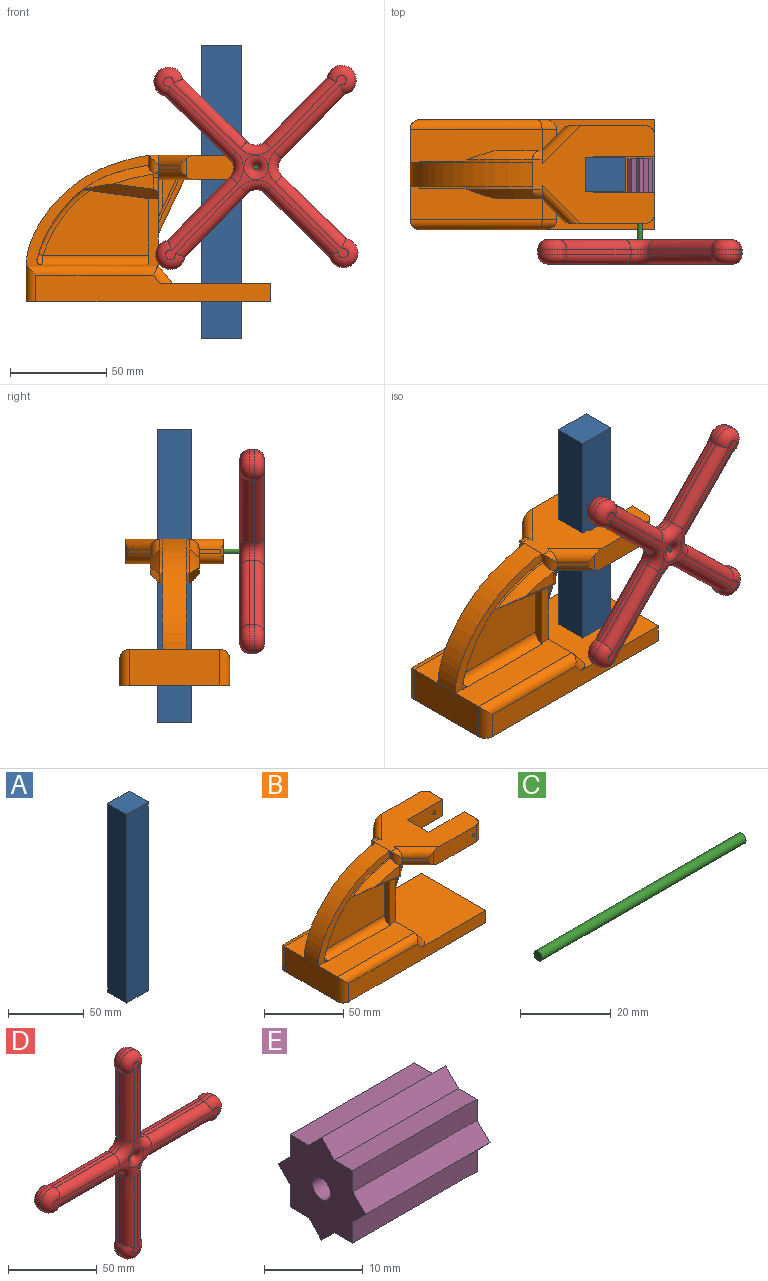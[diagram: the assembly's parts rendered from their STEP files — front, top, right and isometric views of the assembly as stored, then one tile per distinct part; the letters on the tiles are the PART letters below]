
ASSEMBLY  parts=5 mates=4
PART A: 6 faces, bbox 20.3x17.8x152.4 mm
  f0: plane 152.4x20.32mm, normal (0,1,0), area 3096.8mm2, adj f1,f3,f4,f5
  f1: plane 20.32x17.78mm, normal (0,0,1), area 361.3mm2, adj f0,f2,f4,f5
  f2: plane 152.4x20.32mm, normal (0,-1,0), area 3096.8mm2, adj f1,f3,f4,f5
  f3: plane 20.32x17.78mm, normal (0,0,-1), area 361.3mm2, adj f0,f2,f4,f5
  f4: plane 152.4x17.78mm, normal (1,0,0), area 2709.7mm2, adj f0,f1,f2,f3
  f5: plane 152.4x17.78mm, normal (-1,0,0), area 2709.7mm2, adj f0,f1,f2,f3
PART B: 93 faces, bbox 129.2x60.2x85.1 mm
  f0: plane 47.9x22.57mm, normal (1,0,0), area 413.4mm2, adj f1,f2,f12,f37,f38,f39,f45,f50
  f1: plane 58.93x51.31mm, normal (0,0,-1), area 1893.8mm2, adj f0,f2,f3,f57,f58,f59,f62,f67
  f2: plane 21.89x11.58mm, normal (-0.9,0,0.43), area 68.6mm2, adj f0,f1,f76,f78,f83
  f3: plane 12.7x10.8mm, normal (1,0,0), area 137.1mm2, adj f1,f46,f69,f71
  f4: plane 68.58x17.15mm, normal (0,0,1), area 1138.7mm2, adj f6,f7,f8,f12,f19,f22,f33,f38
  f5: plane 68.58x17.15mm, normal (0,0,1), area 1138.7mm2, adj f8,f12,f15,f16,f20,f25,f32,f37
  f6: plane 0.64x0.04mm, normal (1,0,0), area 0mm2, adj f4,f19,f38
  f7: extruded ~0.64x0.04mm, area 0mm2, adj f4,f19,f33
  f8: plane 46.99x19.05mm, normal (-1,0,0), area 895.2mm2, adj f4,f5,f9,f23,f26,f30
  f9: plane 127x57.15mm, normal (0,0,-1), area 7247mm2, adj f8,f10,f13,f14,f23,f26
  f10: plane 57.15x9.53mm, normal (1,0,0), area 544.4mm2, adj f9,f11,f13,f14
  f11: plane 59.01x58.86mm, normal (0,0,1), area 2917.4mm2, adj f10,f12,f13,f14,f21,f24
  f12: plane 46.99x9.53mm, normal (0.78,0,0.62), area 573.2mm2, adj f0,f4,f5,f11,f21,f24
  f13: plane 121.92x13.97mm, normal (0,-1,0), area 1440.6mm2, adj f9,f10,f11,f24,f25,f26
  f14: plane 121.92x13.97mm, normal (0,1,0), area 1440.6mm2, adj f9,f10,f11,f21,f22,f23
  f15: plane 0.64x0.04mm, normal (1,0,0), area 0mm2, adj f5,f20,f37
  f16: extruded ~0.64x0.04mm, area 0mm2, adj f5,f20,f32
  f17: plane 54.64x33.76mm, normal (0,-1,0), area 1467.7mm2, adj f20,f27,f29,f79
  f18: plane 54.64x33.76mm, normal (0,1,0), area 1467.7mm2, adj f19,f36,f44,f81
  f19: cylinder r=5.08mm len=58.42mm, axis (1,0,0), area 440.8mm2, adj f4,f6,f7,f18,f33,f36,f82
  f20: cylinder r=5.08mm len=58.42mm, axis (-1,0,0), area 440.8mm2, adj f5,f15,f16,f17,f29,f32,f80
  f21: cylinder r=5.08mm len=12.7mm, axis (-0.62,0,0.78), area 71.4mm2, adj f11,f12,f14,f22
  f22: cylinder r=5.08mm len=68.58mm, axis (-1,0,0), area 517.2mm2, adj f4,f14,f21,f23
  f23: cylinder r=5.08mm len=19.05mm, axis (0,0,-1), area 131.7mm2, adj f8,f9,f14,f22
  f24: cylinder r=5.08mm len=12.7mm, axis (0.62,0,-0.78), area 71.4mm2, adj f11,f12,f13,f25
  f25: cylinder r=5.08mm len=68.58mm, axis (1,0,0), area 517.2mm2, adj f5,f13,f24,f26
  f26: cylinder r=5.08mm len=19.05mm, axis (0,0,1), area 131.7mm2, adj f8,f9,f13,f25
  f27: plane 35.02x6.64mm, normal (-0.14,0,-0.99), area 194.7mm2, adj f17,f28,f29,f39,f43,f52,f79
  f28: extruded ~36.1x23.66mm, area 81.2mm2, adj f27,f32,f79,f80
  f29: plane 34.61x4.45mm, normal (-1,0,0), area 148.5mm2, adj f17,f20,f27,f37
  f30: extruded ~63.5x57.15mm, area 1168.6mm2, adj f8,f32,f33,f46
  f31: extruded ~36.1x23.66mm, area 81.2mm2, adj f33,f44,f81,f82
  f32: plane 63.96x57.61mm, normal (0,-1,0), area 447.1mm2, adj f5,f16,f20,f28,f30,f34,f43,f80
  f33: plane 63.96x57.61mm, normal (0,1,0), area 447.1mm2, adj f4,f7,f19,f30,f31,f35,f42,f82
  f34: plane 5.08x1.27mm, normal (-1,0,0), area 6.5mm2, adj f32,f43,f46,f55
  f35: extruded ~34.1x12.76mm, area 46.7mm2, adj f33,f42,f44,f49
  f36: plane 34.61x4.45mm, normal (-1,0,0), area 148.5mm2, adj f18,f19,f38,f44
  f37: plane 34.65x5.08mm, normal (0,-1,0), area 176mm2, adj f0,f5,f15,f29,f39
  f38: plane 34.65x5.08mm, normal (0,1,0), area 176mm2, adj f0,f4,f6,f36,f45
  f39: plane 5.08x1.96mm, normal (0,0,-1), area 8.2mm2, adj f0,f27,f37,f52
  f40: plane 9.32x7.22mm, normal (1,0,0), area 2.3mm2, adj f46,f56,f65
  f41: plane 9.32x7.22mm, normal (1,0,0), area 2.3mm2, adj f46,f54,f63
  f42: plane 5.08x1.27mm, normal (-1,0,0), area 6.5mm2, adj f33,f35,f46,f53
  f43: extruded ~34.1x12.76mm, area 46.7mm2, adj f27,f32,f34,f51
  f44: plane 35.02x6.64mm, normal (-0.14,0,-0.99), area 194.7mm2, adj f18,f31,f35,f36,f45,f50,f81
  f45: plane 5.08x1.96mm, normal (0,0,-1), area 8.2mm2, adj f0,f38,f44,f50
  f46: plane 63.5x50.8mm, normal (0,0,1), area 2033.9mm2, adj f3,f30,f34,f40,f41,f42,f54,f56
  f47: plane 22.05x8.82mm, normal (0,-1,0), area 89.7mm2, adj f51,f52,f87,f88
  f48: plane 22.05x8.82mm, normal (0,1,0), area 89.7mm2, adj f49,f50,f89,f90
  f49: bspline ~38.17x17.36mm, area 205.8mm2, adj f35,f48,f50,f53,f89
  f50: plane 40.23x8.67mm, normal (-0.1,0.71,-0.7), area 226.6mm2, adj f0,f44,f45,f48,f49,f90
  f51: bspline ~39.92x18.11mm, area 205.8mm2, adj f43,f47,f52,f55,f87
  f52: plane 40.24x8.68mm, normal (-0.1,-0.71,-0.7), area 226.7mm2, adj f0,f27,f39,f47,f51,f88
  f53: cylinder r=5.08mm len=9.41mm, axis (0,0,-1), area 44.4mm2, adj f42,f49,f54,f61,f89
  f54: cylinder r=5.08mm len=5.08mm, axis (-1,0,0), area 20.3mm2, adj f41,f46,f53
  f55: cylinder r=5.08mm len=9.41mm, axis (0,0,1), area 44.4mm2, adj f34,f51,f56,f60,f87
  f56: cylinder r=5.08mm len=5.08mm, axis (1,0,0), area 20.3mm2, adj f40,f46,f55
  f57: plane 12.7x10.8mm, normal (1,0,0), area 137.1mm2, adj f1,f46,f68,f70
  f58: plane 38.84x13mm, normal (0,-1,0), area 479.6mm2, adj f1,f46,f65,f66,f67,f69,f91
  f59: plane 38.84x13mm, normal (0,1,0), area 479.6mm2, adj f1,f46,f62,f63,f64,f68,f92
  f60: plane 11.21x11.21mm, normal (-0.71,-0.71,0), area 40.3mm2, adj f55,f65,f66,f67
  f61: plane 11.21x11.21mm, normal (-0.71,0.71,0), area 40.3mm2, adj f53,f62,f63,f64
  f62: cylinder r=5.08mm len=23.48mm, axis (-0.71,-0.71,0), area 171.4mm2, adj f0,f1,f59,f61,f64,f89
  f63: cylinder r=5.08mm len=23.48mm, axis (-0.71,-0.71,0), area 175.5mm2, adj f41,f46,f59,f61,f64
  f64: cylinder r=5.08mm len=9.72mm, axis (0,0,-1), area 24.5mm2, adj f59,f61,f62,f63
  f65: cylinder r=5.08mm len=23.48mm, axis (-0.71,0.71,0), area 175.5mm2, adj f40,f46,f58,f60,f66
  f66: cylinder r=5.08mm len=9.72mm, axis (0,0,1), area 24.5mm2, adj f58,f60,f65,f67
  f67: cylinder r=5.08mm len=23.48mm, axis (-0.71,0.71,0), area 171.4mm2, adj f0,f1,f58,f60,f66,f87
  f68: cylinder r=5.08mm len=12.7mm, axis (0,0,1), area 101.3mm2, adj f1,f46,f57,f59
  f69: cylinder r=5.08mm len=12.7mm, axis (0,0,-1), area 101.3mm2, adj f1,f3,f46,f58
  f70: plane 31.75x12.7mm, normal (0,-1,0), area 398.2mm2, adj f1,f46,f57,f72,f92
  f71: plane 31.75x12.7mm, normal (0,1,0), area 398.2mm2, adj f1,f3,f46,f72,f91
  f72: plane 19.05x12.7mm, normal (1,0,0), area 241.9mm2, adj f1,f46,f70,f71
  f73: plane 21.89x11.58mm, normal (-0.9,0,0.43), area 68.6mm2, adj f0,f1,f75,f77,f84
  f74: plane 28.68x13.63mm, normal (0.9,0,-0.43), area 129mm2, adj f0,f1,f85,f86
  f75: plane 22.76x10.81mm, normal (0,-1,0), area 31.4mm2, adj f0,f1,f73,f86
  f76: plane 22.76x10.81mm, normal (0,1,0), area 31.4mm2, adj f0,f1,f2,f85
  f77: plane 14.3x6.79mm, normal (0,-1,0), area 48.5mm2, adj f1,f73,f84
  f78: plane 14.3x6.79mm, normal (0,1,0), area 48.5mm2, adj f1,f2,f83
  f79: bspline ~60.99x57.21mm, area 167.4mm2, adj f17,f27,f28,f80
  f80: bspline ~6.54x5.32mm, area 26.1mm2, adj f20,f28,f32,f79
  f81: bspline ~60.99x57.21mm, area 167.4mm2, adj f18,f31,f44,f82
  f82: bspline ~6.54x5.32mm, area 26.1mm2, adj f19,f31,f33,f81
  f83: cylinder r=2.54mm len=19.64mm, axis (0,0,-1), area 67.7mm2, adj f0,f1,f2,f78
  f84: cylinder r=2.54mm len=19.64mm, axis (0,0,1), area 67.7mm2, adj f0,f1,f73,f77
  f85: cylinder r=2.54mm len=29.77mm, axis (0.43,0,0.9), area 113.6mm2, adj f0,f1,f74,f76
  f86: cylinder r=2.54mm len=29.77mm, axis (-0.43,0,-0.9), area 113.6mm2, adj f0,f1,f74,f75
  f87: bspline ~4.48x2.81mm, area 6.4mm2, adj f47,f51,f55,f67,f88
  f88: cylinder r=2.54mm len=9.13mm, axis (0,0,-1), area 30.6mm2, adj f0,f47,f52,f87
  f89: bspline ~4.48x2.81mm, area 7.3mm2, adj f48,f49,f53,f62,f90
  f90: cylinder r=2.54mm len=9.13mm, axis (0,0,1), area 30.6mm2, adj f0,f48,f50,f89
  f91: cylinder r=1.27mm len=15.88mm, axis (0,-1,0), area 126.7mm2, adj f58,f71
  f92: cylinder r=1.27mm len=15.88mm, axis (0,-1,0), area 126.7mm2, adj f59,f70
PART C: 3 faces, bbox 63.5x2.5x2.5 mm
  f0: cylinder r=1.27mm len=63.5mm, axis (-1,0,0), area 506.7mm2, adj f1,f2
  f1: plane 2.54x2.54mm, normal (1,0,0), area 5.1mm2, adj f0
  f2: plane 2.54x2.54mm, normal (-1,0,0), area 5.1mm2, adj f0
PART D: 53 faces, bbox 142.2x12.7x142.2 mm
  f0: cylinder r=7.62mm len=15.24mm, axis (0,1,0), area 83.5mm2, adj f1,f15,f32,f49
  f1: plane 46.59x2.54mm, normal (1,0,0), area 118.3mm2, adj f0,f2,f30,f47
  f2: cylinder r=6.35mm len=6.35mm, axis (0,1,0), area 25.3mm2, adj f1,f3,f28,f45
  f3: plane 46.59x2.54mm, normal (0,0,-1), area 118.3mm2, adj f2,f4,f26,f43
  f4: cylinder r=7.62mm len=15.24mm, axis (0,1,0), area 83.5mm2, adj f3,f5,f24,f41
  f5: plane 46.59x2.54mm, normal (0,0,1), area 118.3mm2, adj f4,f6,f22,f39
  f6: cylinder r=6.35mm len=6.35mm, axis (0,1,0), area 25.3mm2, adj f5,f7,f20,f37
  f7: plane 46.59x2.54mm, normal (1,0,0), area 118.3mm2, adj f6,f8,f19,f36
  f8: cylinder r=7.62mm len=15.24mm, axis (0,1,0), area 83.5mm2, adj f7,f9,f21,f38
  f9: plane 46.59x2.54mm, normal (-1,0,0), area 118.3mm2, adj f8,f10,f23,f40
  f10: cylinder r=6.35mm len=6.35mm, axis (0,1,0), area 25.3mm2, adj f9,f11,f25,f42
  f11: plane 46.59x2.54mm, normal (0,0,1), area 118.3mm2, adj f10,f12,f27,f44
  f12: cylinder r=7.62mm len=15.24mm, axis (0,1,0), area 83.5mm2, adj f11,f13,f29,f46
  f13: plane 46.59x2.54mm, normal (0,0,-1), area 118.3mm2, adj f12,f14,f31,f48
  f14: cylinder r=6.35mm len=6.35mm, axis (0,1,0), area 25.3mm2, adj f13,f15,f33,f50
  f15: plane 46.59x2.54mm, normal (-1,0,0), area 118.3mm2, adj f0,f14,f34,f51
  f16: cylinder r=1.27mm len=2.54mm, axis (0,1,0), area 20.3mm2, adj f35,f52
  f17: plane 132.08x132.08mm, normal (0,-1,0), area 680.6mm2, adj f36,f37,f38,f39,f40,f41,f42,f43
  f18: plane 132.08x132.08mm, normal (0,1,0), area 680.6mm2, adj f19,f20,f21,f22,f23,f24,f25,f26
  f19: cylinder r=5.08mm len=48.6mm, axis (0,0,1), area 376.9mm2, adj f7,f18,f20,f21
  f20: torus R=11.43mm, axis (0,-1,0), area 102.7mm2, adj f6,f18,f19,f22
  f21: torus R=2.54mm, axis (0,-1,0), area 206.5mm2, adj f8,f18,f19,f23
  f22: cylinder r=5.08mm len=48.6mm, axis (-1,0,0), area 376.9mm2, adj f5,f18,f20,f24
  f23: cylinder r=5.08mm len=48.6mm, axis (0,0,-1), area 376.9mm2, adj f9,f18,f21,f25
  f24: torus R=2.54mm, axis (0,-1,0), area 206.5mm2, adj f4,f18,f22,f26
  f25: torus R=11.43mm, axis (0,-1,0), area 102.7mm2, adj f10,f18,f23,f27
  f26: cylinder r=5.08mm len=48.6mm, axis (1,0,0), area 376.9mm2, adj f3,f18,f24,f28
  f27: cylinder r=5.08mm len=48.6mm, axis (-1,0,0), area 376.9mm2, adj f11,f18,f25,f29
  f28: torus R=11.43mm, axis (0,-1,0), area 102.7mm2, adj f2,f18,f26,f30
  f29: torus R=2.54mm, axis (0,-1,0), area 206.5mm2, adj f12,f18,f27,f31
  f30: cylinder r=5.08mm len=48.6mm, axis (0,0,1), area 376.9mm2, adj f1,f18,f28,f32
  f31: cylinder r=5.08mm len=48.6mm, axis (1,0,0), area 376.9mm2, adj f13,f18,f29,f33
  f32: torus R=2.54mm, axis (0,-1,0), area 206.5mm2, adj f0,f18,f30,f34
  f33: torus R=11.43mm, axis (0,-1,0), area 102.7mm2, adj f14,f18,f31,f34
  f34: cylinder r=5.08mm len=48.6mm, axis (0,0,-1), area 376.9mm2, adj f15,f18,f32,f33
  f35: torus R=6.35mm, axis (0,-1,0), area 156.2mm2, adj f16,f18
  f36: cylinder r=5.08mm len=48.6mm, axis (0,0,-1), area 376.9mm2, adj f7,f17,f37,f38
  f37: torus R=11.43mm, axis (0,-1,0), area 102.7mm2, adj f6,f17,f36,f39
  f38: torus R=2.54mm, axis (0,-1,0), area 206.5mm2, adj f8,f17,f36,f40
  f39: cylinder r=5.08mm len=48.6mm, axis (1,0,0), area 376.9mm2, adj f5,f17,f37,f41
  f40: cylinder r=5.08mm len=48.6mm, axis (0,0,1), area 376.9mm2, adj f9,f17,f38,f42
  f41: torus R=2.54mm, axis (0,-1,0), area 206.5mm2, adj f4,f17,f39,f43
  f42: torus R=11.43mm, axis (0,-1,0), area 102.7mm2, adj f10,f17,f40,f44
  f43: cylinder r=5.08mm len=48.6mm, axis (-1,0,0), area 376.9mm2, adj f3,f17,f41,f45
  f44: cylinder r=5.08mm len=48.6mm, axis (1,0,0), area 376.9mm2, adj f11,f17,f42,f46
  f45: torus R=11.43mm, axis (0,-1,0), area 102.7mm2, adj f2,f17,f43,f47
  f46: torus R=2.54mm, axis (0,-1,0), area 206.5mm2, adj f12,f17,f44,f48
  f47: cylinder r=5.08mm len=48.6mm, axis (0,0,-1), area 376.9mm2, adj f1,f17,f45,f49
  f48: cylinder r=5.08mm len=48.6mm, axis (-1,0,0), area 376.9mm2, adj f13,f17,f46,f50
  f49: torus R=2.54mm, axis (0,-1,0), area 206.5mm2, adj f0,f17,f47,f51
  f50: torus R=11.43mm, axis (0,-1,0), area 102.7mm2, adj f14,f17,f48,f51
  f51: cylinder r=5.08mm len=48.6mm, axis (0,0,1), area 376.9mm2, adj f15,f17,f49,f50
  f52: torus R=6.35mm, axis (0,-1,0), area 156.2mm2, adj f16,f17
PART E: 19 faces, bbox 17.8x12.6x12.7 mm
  f0: plane 17.78x1.86mm, normal (0,-0.71,-0.71), area 46.8mm2, adj f1,f15,f17,f18
  f1: plane 17.78x1.86mm, normal (0,0.71,-0.7), area 46.3mm2, adj f0,f2,f17,f18
  f2: plane 17.78x2.67mm, normal (0,0,-1), area 47.4mm2, adj f1,f3,f17,f18
  f3: plane 17.78x2.72mm, normal (0,1,0), area 48.4mm2, adj f2,f4,f17,f18
  f4: plane 17.78x1.77mm, normal (0,0.71,-0.7), area 44mm2, adj f3,f5,f17,f18
  f5: plane 17.78x1.77mm, normal (0,0.71,0.7), area 44mm2, adj f4,f6,f17,f18
  f6: plane 17.78x2.72mm, normal (0,1,0), area 48.4mm2, adj f5,f7,f17,f18
  f7: plane 17.78x2.67mm, normal (0,0,1), area 47.4mm2, adj f6,f8,f17,f18
  f8: plane 17.78x1.86mm, normal (0,0.71,0.7), area 46.3mm2, adj f7,f9,f17,f18
  f9: plane 17.78x1.86mm, normal (0,-0.71,0.71), area 46.8mm2, adj f8,f10,f17,f18
  f10: plane 17.78x2.63mm, normal (0,0,1), area 46.8mm2, adj f9,f11,f17,f18
  f11: plane 17.78x2.63mm, normal (0,-1,0), area 46.8mm2, adj f10,f12,f17,f18
  f12: plane 17.78x1.86mm, normal (0,-0.71,0.71), area 46.8mm2, adj f11,f13,f17,f18
  f13: plane 17.78x1.86mm, normal (0,-0.71,-0.71), area 46.8mm2, adj f12,f14,f17,f18
  f14: plane 17.78x2.63mm, normal (0,-1,0), area 46.8mm2, adj f13,f15,f17,f18
  f15: plane 17.78x2.63mm, normal (0,0,-1), area 46.8mm2, adj f0,f14,f17,f18
  f16: cylinder r=1.27mm len=17.78mm, axis (-1,0,0), area 141.9mm2, adj f17,f18
  f17: plane 12.7x12.57mm, normal (1,0,0), area 89mm2, adj f0,f1,f2,f3,f4,f5,f6,f7
  f18: plane 12.7x12.57mm, normal (-1,0,0), area 89mm2, adj f0,f1,f2,f3,f4,f5,f6,f7
PLACE A rot(axis=(0,1,0),180deg) t=(17.01,103.34,110.83)mm
PLACE B t=(-31.12,60.04,36.15)mm fixed
PLACE C rot(axis=(0.35,0.35,0.87),98.2deg) t=(8.42,14.96,169.31)mm
PLACE D rot(axis=(0,-1,0),45.6deg) t=(24.76,26.17,96.47)mm
PLACE E rot(axis=(0.68,-0.68,-0.28),149deg) t=(-23.51,68.3,88.51)mm
MATE fastened C.f0 <-> E.f16  axis (0,1,0) through (24.76,78.46,96.47)mm
MATE slider B.f11 <-> A.f1  axis (0,0,1) through (6.85,60.04,36.15)mm
MATE fastened D.f16 <-> C.f0  axis (0,-1,0) through (24.76,14.96,96.47)mm
MATE revolute E.f16 <-> B.f91  axis (0,-1,0) through (24.76,50.52,96.47)mm
